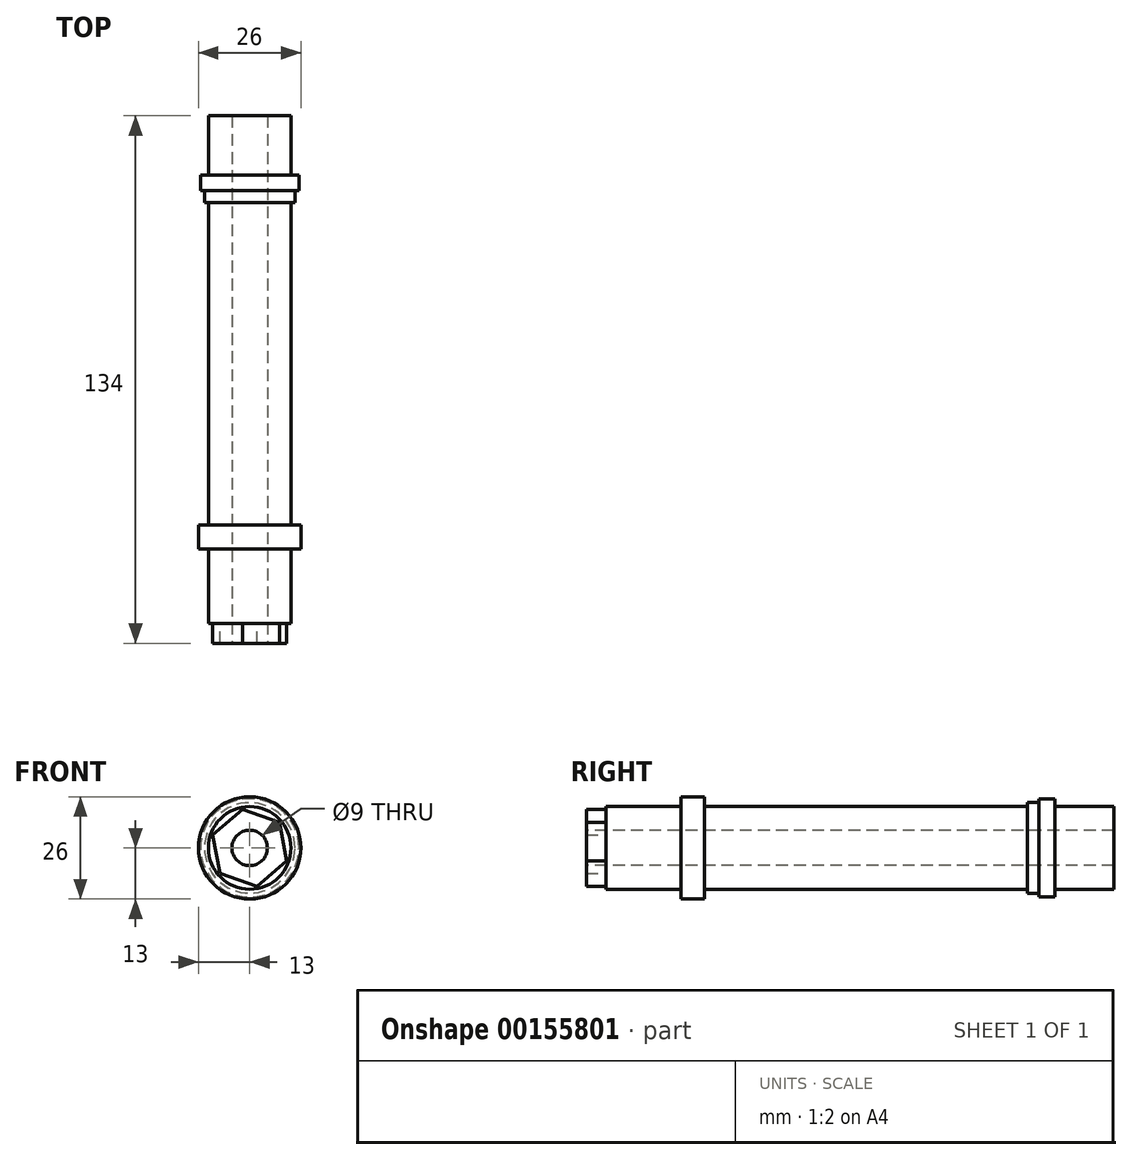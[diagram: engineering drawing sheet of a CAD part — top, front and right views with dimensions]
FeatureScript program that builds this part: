
annotation { "Feature Type Name" : "Feature", "Feature Type Description" : "" }
export const myFeature = defineFeature(function(context is Context, id is Id, definition is map)
    precondition{}
    {
        {
            var Q0;
            Q0=qCreatedBy(makeId("Front.planeOp"),FACE);
            var sketch = newSketch(context, id + "F0", { "sketchPlane" : qUnion([Q0])});
            skLineSegment(sketch, "E0", {"start": v(0, 59.3) * mm, "end": v(0, -56.41) * mm, "construction": true});
            skLineSegment(sketch, "E1", {"start": v(58.11, 0) * mm, "end": v(-58.38, 0) * mm, "construction": true});
            skCircle(sketch, "E2", {"center": v(0, 0) * mm, "radius": 13 * mm});
            skSolve(sketch);
        }
        {
            var Q0;
            Q0=qSketchRegion(id+"F0",true);
            extrude(context, id + "F1", {"entities" : qUnion([Q0]), "depth" : 6 * mm});
        }
        {
            var Q0;
            Q0=makeQuery(id+"F1.opExtrude","CAP_FACE",FACE,{"disambiguationData":[OSD([sQuery(id+"F0.wireOp",EDGE,"E2")])],"isStart":false});
            var sketch = newSketch(context, id + "F2", { "sketchPlane" : qUnion([Q0])});
            skCircle(sketch, "E3", {"center": v(0, 0) * mm, "radius": 10.5 * mm});
            skSolve(sketch);
        }
        {
            var Q0;
            Q0=qSketchRegion(id+"F2",true);
            extrude(context, id + "F3", {"entities" : qUnion([Q0]), "operationType" : NewBodyOperationType.ADD, "depth" : 19 * mm, "hasSecondDirection" : true, "secondDirectionOppositeDirection" : true, "secondDirectionDepth" : 110 * mm});
        }
        {
            var Q0;
            Q0=makeQuery(id+"F3.opExtrude","CAP_FACE",FACE,{"disambiguationData":[OSD([sQuery(id+"F2.wireOp",EDGE,"E3")])],"isStart":false});
            var sketch = newSketch(context, id + "F4", { "sketchPlane" : qUnion([Q0])});
            skCircle(sketch, "E4", {"center": v(0, 0) * mm, "radius": 4.5 * mm});
            skSolve(sketch);
        }
        {
            var Q0;
            Q0=makeQuery(id+"F3.opExtrude","CAP_FACE",FACE,{"disambiguationData":[OSD([sQuery(id+"F2.wireOp",EDGE,"E3")])],"isStart":true});
            var sketch = newSketch(context, id + "F5", { "sketchPlane" : qUnion([Q0])});
            skCircle(sketch, "E5", {"center": v(0, 0) * mm, "radius": 11.5 * mm});
            skCircle(sketch, "E6", {"center": v(0, 0) * mm, "radius": 10.5 * mm});
            skSolve(sketch);
        }
        {
            var Q0;
            Q0=qSketchRegion(id+"F5",true);
            extrude(context, id + "F6", {"entities" : qUnion([Q0]), "operationType" : NewBodyOperationType.ADD, "oppositeDirection" : true, "depth" : 22 * mm, "hasSecondDirection" : true, "secondDirectionOppositeDirection" : true, "secondDirectionDepth" : 19 * mm});
        }
        {
            var Q0;
            Q0=makeQuery(id+"F3.opExtrude","CAP_FACE",FACE,{"disambiguationData":[OSD([sQuery(id+"F2.wireOp",EDGE,"E3")])],"isStart":true});
            var sketch = newSketch(context, id + "F7", { "sketchPlane" : qUnion([Q0])});
            skCircle(sketch, "E7", {"center": v(0, 0) * mm, "radius": 12.5 * mm});
            skCircle(sketch, "E8", {"center": v(0, 0) * mm, "radius": 10.5 * mm});
            skSolve(sketch);
        }
        {
            var Q0;
            Q0=qSketchRegion(id+"F7",true);
            extrude(context, id + "F8", {"entities" : qUnion([Q0]), "operationType" : NewBodyOperationType.ADD, "oppositeDirection" : true, "depth" : 19 * mm, "hasSecondDirection" : true, "secondDirectionOppositeDirection" : true, "secondDirectionDepth" : 15 * mm});
        }
        {
            var Q0;
            Q0=makeQuery(id+"F4.imprint","IMPRINT",FACE,{"disambiguationData":[TD([[makeQuery(id+"F4.imprint","IMPRINT",EDGE,{"derivedFrom":sQuery(id+"F4.wireOp",EDGE,"E4")}),-1.0]])]});
            var sketch = newSketch(context, id + "F9", { "sketchPlane" : qUnion([Q0])});
            skCircle(sketch, "E9.cCircle", {"center": v(0, 0) * mm, "radius": 8.62 * mm, "construction": true});
            skLineSegment(sketch, "E9.0", {"start": v(7.55, 6.48) * mm, "end": v(9.39, -3.3) * mm});
            skLineSegment(sketch, "E9.1", {"start": v(9.39, -3.3) * mm, "end": v(1.83, -9.78) * mm});
            skLineSegment(sketch, "E9.2", {"start": v(1.83, -9.78) * mm, "end": v(-7.55, -6.48) * mm});
            skLineSegment(sketch, "E9.3", {"start": v(-7.55, -6.48) * mm, "end": v(-9.39, 3.3) * mm});
            skLineSegment(sketch, "E9.4", {"start": v(-9.39, 3.3) * mm, "end": v(-1.83, 9.78) * mm});
            skLineSegment(sketch, "E9.5", {"start": v(-1.83, 9.78) * mm, "end": v(7.55, 6.48) * mm});
            skPoint(sketch, "E9.0.midPoint", {"position": v(8.47, 1.59) * mm});
            skSolve(sketch);
        }
        {
            var Q0;
            Q0 = qSketchRegion(id + "F9", true);
            extrude(context, id + "F10", {"entities" : qUnion([Q0]), "operationType" : NewBodyOperationType.ADD, "depth" : 5 * mm});
        }
        {
            var Q0;
            Q0=makeQuery(id+"F10.opExtrude","CAP_FACE",FACE,{"disambiguationData":[OSD([sQuery(id+"F9.wireOp",EDGE,"E9.0"),sQuery(id+"F9.wireOp",EDGE,"E9.1"),sQuery(id+"F9.wireOp",EDGE,"E9.2"),sQuery(id+"F9.wireOp",EDGE,"E9.3"),sQuery(id+"F9.wireOp",EDGE,"E9.4"),sQuery(id+"F9.wireOp",EDGE,"E9.5")])],"isStart":false});
            var sketch = newSketch(context, id + "F11", { "sketchPlane" : qUnion([Q0])});
            skCircle(sketch, "E10", {"center": v(0, 0) * mm, "radius": 4.5 * mm});
            skSolve(sketch);
        }
        {
            var Q0;
            Q0 = qSketchRegion(id + "F11", true);
            extrude(context, id + "F12", {"entities" : qUnion([Q0]), "operationType" : NewBodyOperationType.REMOVE, "oppositeDirection" : true, "depth" : 153 * mm});
        }
    });
